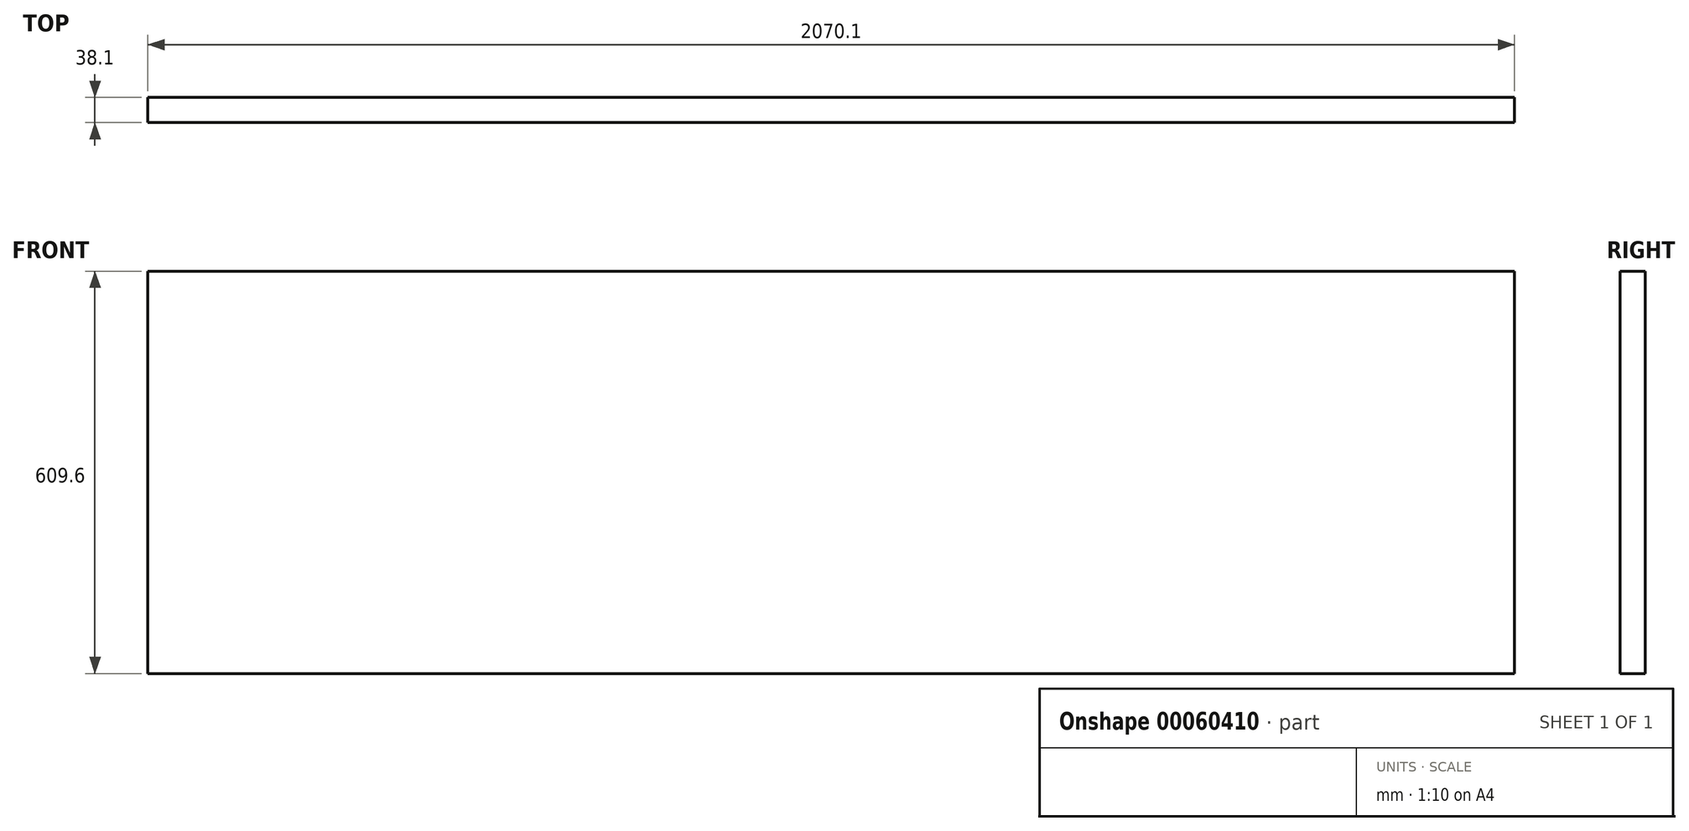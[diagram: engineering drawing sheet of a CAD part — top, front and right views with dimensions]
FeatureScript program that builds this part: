
annotation { "Feature Type Name" : "Feature", "Feature Type Description" : "" }
export const myFeature = defineFeature(function(context is Context, id is Id, definition is map)
    precondition{}
    {
        {
            var Q0;
            Q0=qCreatedBy(makeId("Right.planeOp"),FACE);
            var sketch = newSketch(context, id + "F0", { "sketchPlane" : qUnion([Q0])});
            skLineSegment(sketch, "E0.bottom", {"start": v(0, 0) * mm, "end": v(-38.1, 0) * mm});
            skLineSegment(sketch, "E0.top", {"start": v(0, 609.6) * mm, "end": v(-38.1, 609.6) * mm});
            skLineSegment(sketch, "E0.left", {"start": v(0, 0) * mm, "end": v(0, 609.6) * mm});
            skLineSegment(sketch, "E0.right", {"start": v(-38.1, 0) * mm, "end": v(-38.1, 609.6) * mm});
            skSolve(sketch);
        }
        {
            var Q0;
            Q0=makeQuery(id+"F0.imprint","IMPRINT",FACE,{"disambiguationData":[TD([[makeQuery(id+"F0.imprint","IMPRINT",EDGE,{"derivedFrom":sQuery(id+"F0.wireOp",EDGE,"E0.bottom")}),-1.0]])]});
            extrude(context, id + "F1", {"entities" : qUnion([Q0]), "depth" : 2070.1 * mm});
        }
    });
